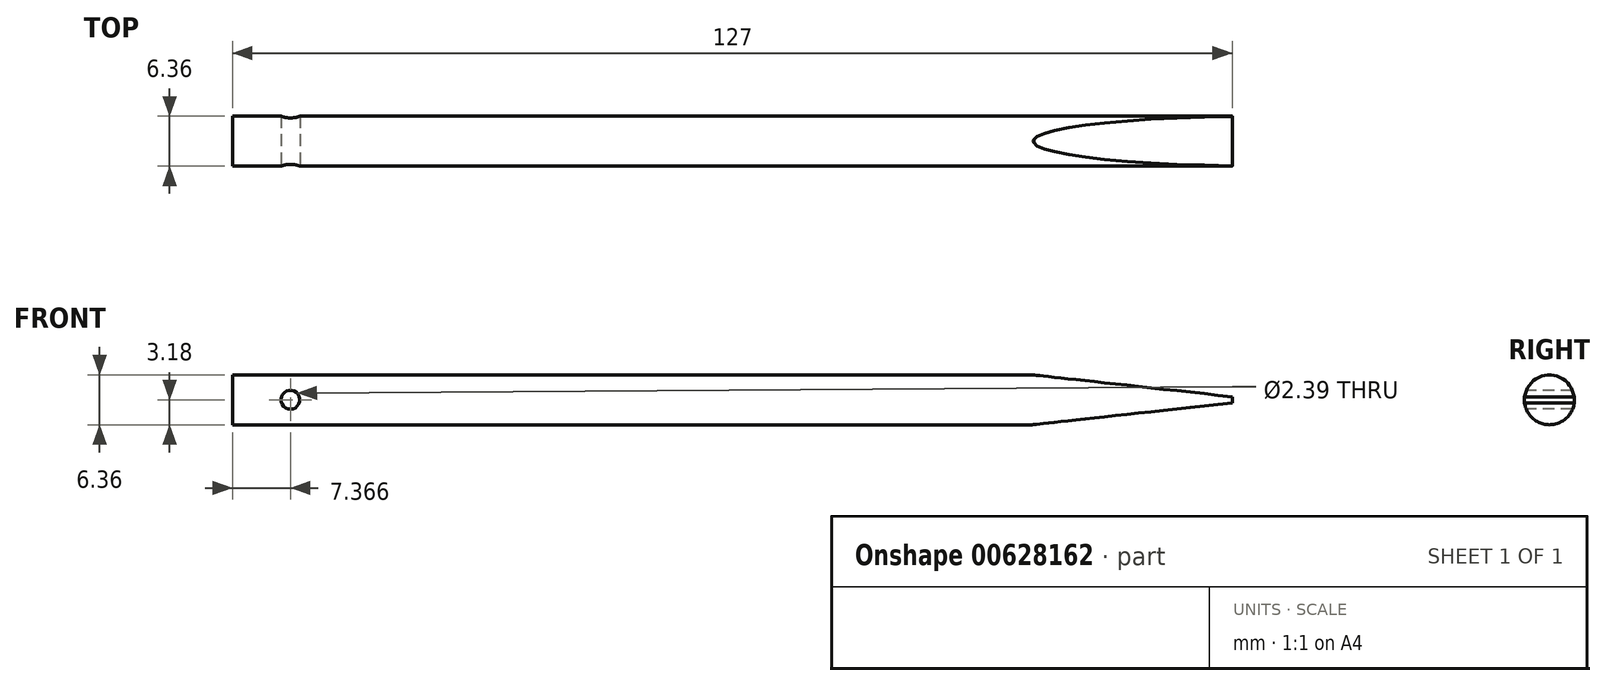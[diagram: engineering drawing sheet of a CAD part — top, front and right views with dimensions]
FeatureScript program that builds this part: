
annotation { "Feature Type Name" : "Feature", "Feature Type Description" : "" }
export const myFeature = defineFeature(function(context is Context, id is Id, definition is map)
    precondition{}
    {
        {
            var Q0;
            Q0=qCreatedBy(makeId("Right.planeOp"),FACE);
            var sketch = newSketch(context, id + "F0", { "sketchPlane" : qUnion([Q0])});
            skCircle(sketch, "E0", {"center": v(0, 0) * mm, "radius": 3.18 * mm});
            skSolve(sketch);
        }
        {
            var Q0;
            Q0=makeQuery(id+"F0.imprint","IMPRINT",FACE,{"disambiguationData":[TD([[makeQuery(id+"F0.imprint","IMPRINT",EDGE,{"derivedFrom":sQuery(id+"F0.wireOp",EDGE,"E0")}),1.0]])]});
            var Q1;
            Q1=sQuery(id+"F0.wireOp",EDGE,"E0");
            extrude(context, id + "F1", {"entities" : qUnion([Q0]), "surfaceEntities" : qUnion([Q1]), "oppositeDirection" : true, "depth" : 127 * mm, "offsetDistance" : 25.4 * mm});
        }
        {
            var Q0;
            Q0=qCreatedBy(makeId("Front.planeOp"),FACE);
            var sketch = newSketch(context, id + "F2", { "sketchPlane" : qUnion([Q0])});
            skCircle(sketch, "E1", {"center": v(-119.63, 0) * mm, "radius": 1.2 * mm});
            skSolve(sketch);
        }
        {
            var Q0;
            Q0=qCreatedBy(makeId("Front.planeOp"),FACE);
            var sketch = newSketch(context, id + "F3", { "sketchPlane" : qUnion([Q0])});
            skLineSegment(sketch, "E2", {"start": v(0, 0) * mm, "end": v(-48.12, 0) * mm, "construction": true});
            skLineSegment(sketch, "E3", {"start": v(0, 0) * mm, "end": v(0, -0.38) * mm});
            skLineSegment(sketch, "E4", {"start": v(0, 0) * mm, "end": v(0, 0.38) * mm});
            skLineSegment(sketch, "E5", {"start": v(0, -0.38) * mm, "end": v(0, -3.18) * mm});
            skLineSegment(sketch, "E6", {"start": v(0, 0.38) * mm, "end": v(0, 3.18) * mm});
            skLineSegment(sketch, "E7", {"start": v(0, 3.18) * mm, "end": v(-25.4, 3.18) * mm});
            skLineSegment(sketch, "E8", {"start": v(-25.4, 3.18) * mm, "end": v(0, 0.38) * mm});
            skLineSegment(sketch, "E9", {"start": v(0, -3.18) * mm, "end": v(-25.4, -3.18) * mm});
            skLineSegment(sketch, "E10", {"start": v(-25.4, -3.18) * mm, "end": v(0, -0.38) * mm});
            skSolve(sketch);
        }
        {
            var Q0;
            Q0 = qSketchRegion(id + "F3", true);
            extrude(context, id + "F4", {"entities" : qUnion([Q0]), "operationType" : NewBodyOperationType.REMOVE, "endBound" : BoundingType.SYMMETRIC, "oppositeDirection" : true, "depth" : 25.4 * mm, "offsetDistance" : 25.4 * mm});
        }
        {
            var Q0;
            Q0 = qSketchRegion(id + "F2", true);
            extrude(context, id + "F5", {"entities" : qUnion([Q0]), "operationType" : NewBodyOperationType.REMOVE, "endBound" : BoundingType.SYMMETRIC, "oppositeDirection" : true, "depth" : 25.4 * mm, "offsetDistance" : 25.4 * mm});
        }
    });
